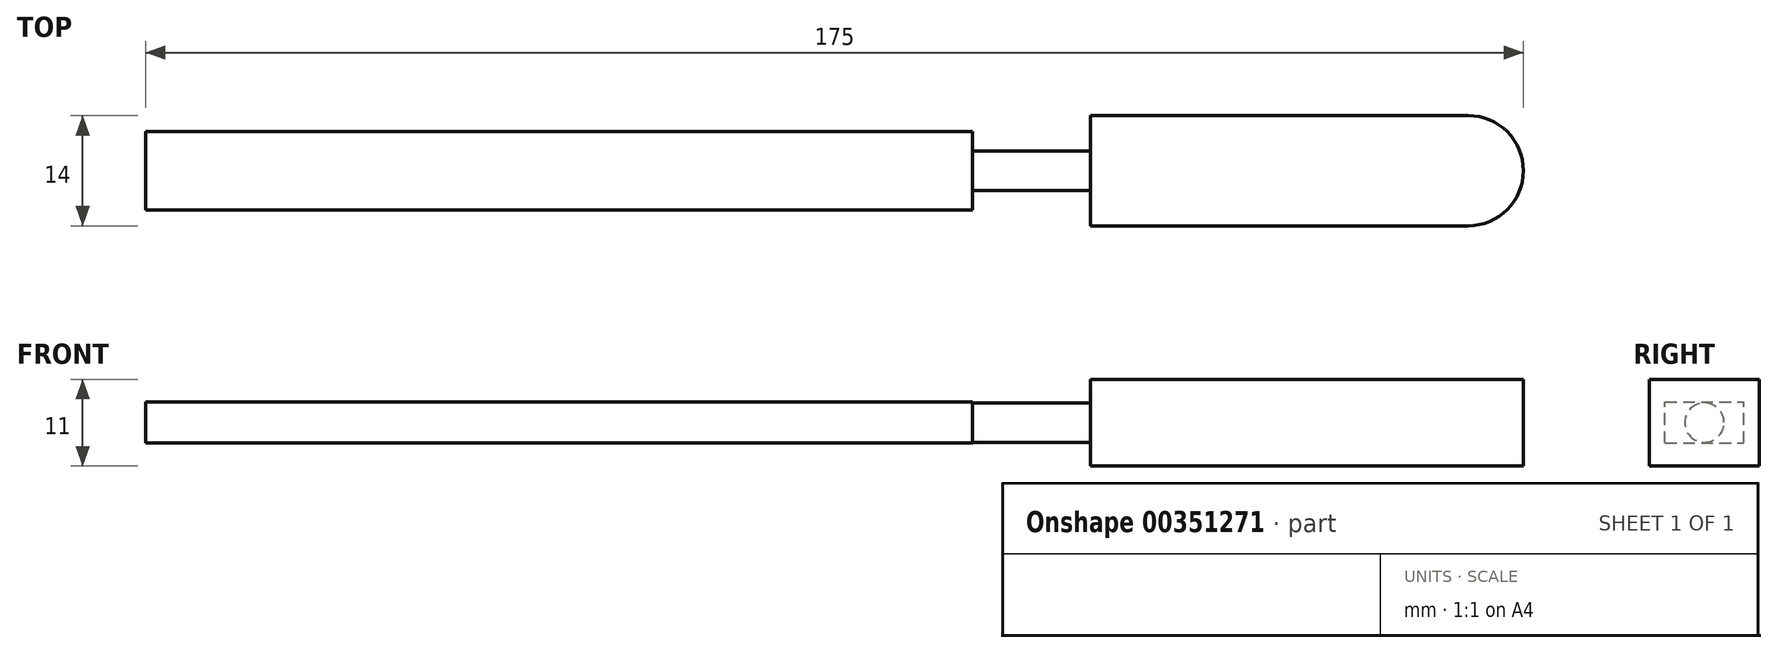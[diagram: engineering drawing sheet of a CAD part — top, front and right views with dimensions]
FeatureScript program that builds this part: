
annotation { "Feature Type Name" : "Feature", "Feature Type Description" : "" }
export const myFeature = defineFeature(function(context is Context, id is Id, definition is map)
    precondition{}
    {
        {
            var Q0;
            Q0=qCreatedBy(makeId("Top.planeOp"),FACE);
            var sketch = newSketch(context, id + "F0", { "sketchPlane" : qUnion([Q0])});
            skLineSegment(sketch, "E0", {"start": v(0, 0) * mm, "end": v(0, 7) * mm});
            skLineSegment(sketch, "E1", {"start": v(0, 7) * mm, "end": v(48, 7) * mm});
            skLineSegment(sketch, "E2", {"start": v(55, 0) * mm, "end": v(55, 0) * mm});
            skLineSegment(sketch, "E3", {"start": v(48, -7) * mm, "end": v(0, -7) * mm});
            skLineSegment(sketch, "E4", {"start": v(0, -7) * mm, "end": v(0, 0) * mm});
            skPoint(sketch, "E5.visualSharp", {"position": v(55, 7) * mm});
            skArc(sketch, "E5.filletArc", {"start": v(55, 0) * mm, "mid": v(52.95, 4.95) * mm, "end": v(48, 7) * mm});
            skPoint(sketch, "E6.visualSharp", {"position": v(55, -7) * mm});
            skArc(sketch, "E6.filletArc", {"start": v(48, -7) * mm, "mid": v(52.95, -4.95) * mm, "end": v(55, 0) * mm});
            skSolve(sketch);
        }
        {
            var Q0;
            Q0 = qSketchRegion(id + "F0", true);
            extrude(context, id + "F1", {"entities" : qUnion([Q0]), "endBound" : BoundingType.SYMMETRIC, "depth" : 11 * mm});
        }
        {
            var Q0;
            Q0=makeQuery(id+"F1.opExtrude","SWEPT_FACE",FACE,{"disambiguationData":[OSD([sQuery(id+"F0.wireOp",EDGE,"E0"),sQuery(id+"F0.wireOp",EDGE,"E4")])]});
            var sketch = newSketch(context, id + "F2", { "sketchPlane" : qUnion([Q0])});
            skCircle(sketch, "E7", {"center": v(0, 0) * mm, "radius": 2.5 * mm});
            skSolve(sketch);
        }
        {
            var Q0;
            Q0 = qSketchRegion(id + "F2", true);
            extrude(context, id + "F3", {"entities" : qUnion([Q0]), "operationType" : NewBodyOperationType.ADD, "depth" : 15 * mm});
        }
        {
            var Q0;
            Q0=makeQuery(id+"F3.opExtrude","CAP_FACE",FACE,{"disambiguationData":[OSD([sQuery(id+"F2.wireOp",EDGE,"E7")])],"isStart":false});
            var sketch = newSketch(context, id + "F4", { "sketchPlane" : qUnion([Q0])});
            skLineSegment(sketch, "E8.bottom", {"start": v(5, -2.6) * mm, "end": v(-5, -2.6) * mm});
            skLineSegment(sketch, "E8.top", {"start": v(5, 2.6) * mm, "end": v(-5, 2.6) * mm});
            skLineSegment(sketch, "E8.left", {"start": v(5, -2.6) * mm, "end": v(5, 2.6) * mm});
            skLineSegment(sketch, "E8.right", {"start": v(-5, -2.6) * mm, "end": v(-5, 2.6) * mm});
            skPoint(sketch, "E8.middle", {"position": v(0, 0) * mm});
            skSolve(sketch);
        }
        {
            var Q0;
            Q0 = qSketchRegion(id + "F4", true);
            extrude(context, id + "F5", {"entities" : qUnion([Q0]), "operationType" : NewBodyOperationType.ADD, "depth" : 105 * mm});
        }
    });
